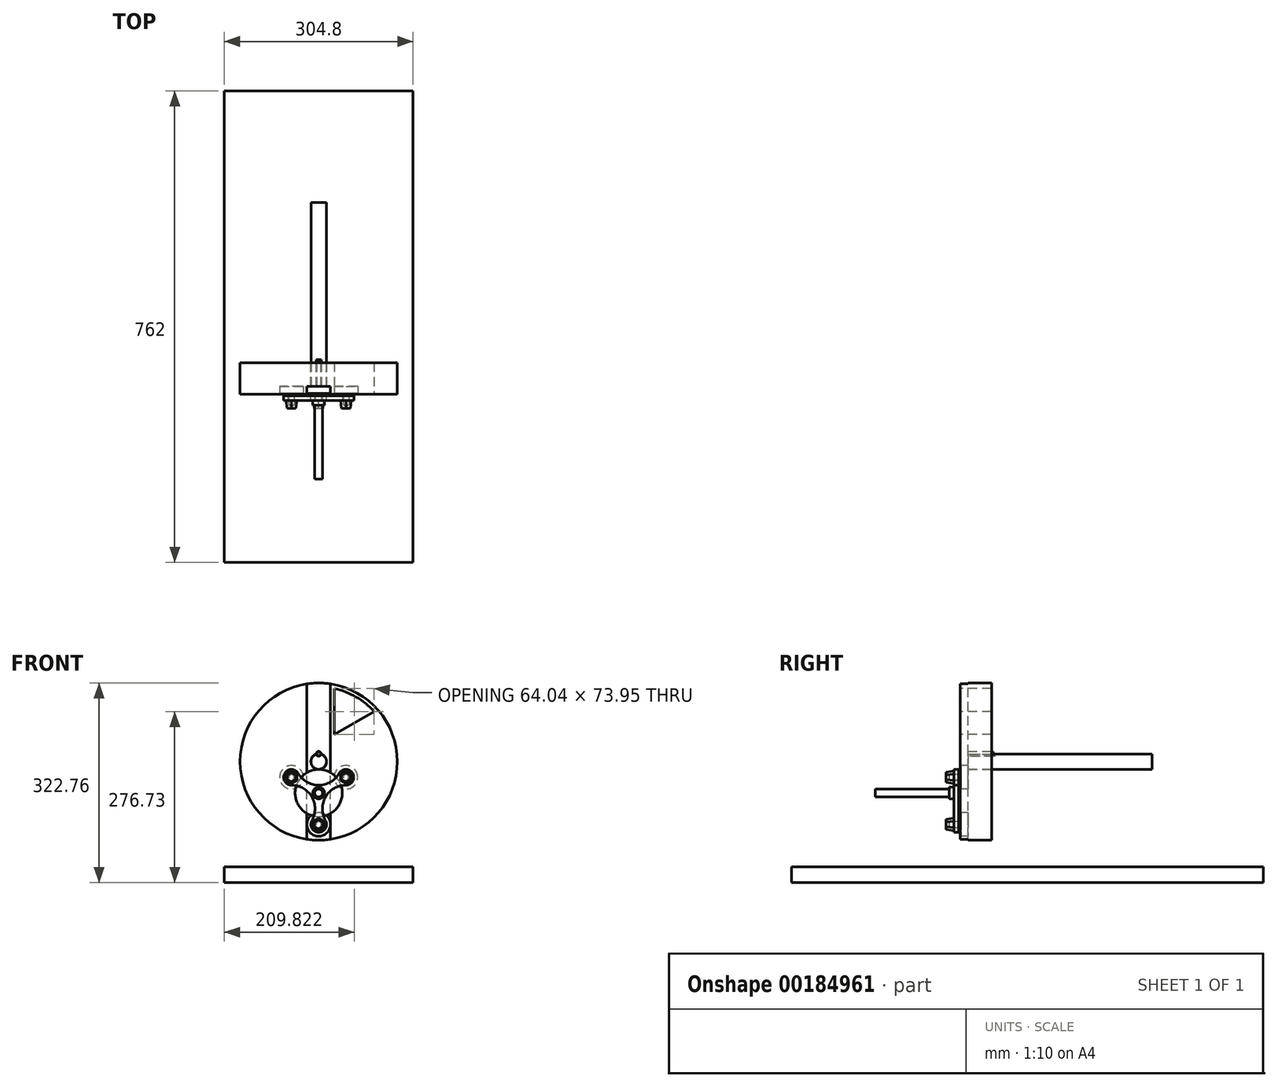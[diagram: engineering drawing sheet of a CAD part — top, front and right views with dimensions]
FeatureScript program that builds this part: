
annotation { "Feature Type Name" : "Feature", "Feature Type Description" : "" }
export const myFeature = defineFeature(function(context is Context, id is Id, definition is map)
    precondition{}
    {
        {
            var Q0;
            Q0=qCreatedBy(makeId("Front.planeOp"),FACE);
            var sketch = newSketch(context, id + "F0", { "sketchPlane" : qUnion([Q0])});
            skCircle(sketch, "E0", {"center": v(0, 0) * mm, "radius": 127 * mm});
            skLineSegment(sketch, "E1", {"start": v(0, 0) * mm, "end": v(0, 12.7) * mm, "construction": true});
            skArc(sketch, "E2", {"start": v(-3.77, 12.13) * mm, "mid": v(0, -12.7) * mm, "end": v(3.77, 12.13) * mm});
            skArc(sketch, "E3", {"start": v(3.77, 12.13) * mm, "mid": v(0, 12.7) * mm, "end": v(-3.77, 12.13) * mm, "construction": true});
            skArc(sketch, "E4", {"start": v(-3.77, 12.13) * mm, "mid": v(0, 8.9) * mm, "end": v(3.77, 12.13) * mm, "construction": true});
            skArc(sketch, "E5", {"start": v(3.77, 12.13) * mm, "mid": v(0, 16.51) * mm, "end": v(-3.77, 12.13) * mm});
            skSolve(sketch);
        }
        {
            var Q0;
            Q0 = qSketchRegion(id + "F0", true);
            extrude(context, id + "F1", {"entities" : qUnion([Q0]), "depth" : 50.8 * mm});
        }
        {
            var Q0;
            Q0=makeQuery(id+"F1.opExtrude","CAP_FACE",FACE,{"disambiguationData":[OSD([sQuery(id+"F0.wireOp",EDGE,"E0")])],"isStart":false});
            var sketch = newSketch(context, id + "F2", { "sketchPlane" : qUnion([Q0])});
            skLineSegment(sketch, "E6", {"start": v(0, -127) * mm, "end": v(0, 147.94) * mm, "construction": true});
            skLineSegment(sketch, "E7.bottom", {"start": v(-19.05, -127) * mm, "end": v(19.05, -127) * mm});
            skLineSegment(sketch, "E7.top", {"start": v(-19.05, 127) * mm, "end": v(19.05, 127) * mm});
            skLineSegment(sketch, "E7.left", {"start": v(-19.05, -127) * mm, "end": v(-19.05, 127) * mm});
            skLineSegment(sketch, "E7.right", {"start": v(19.05, -127) * mm, "end": v(19.05, 127) * mm});
            skSolve(sketch);
        }
        {
            var Q0;
            Q0 = qSketchRegion(id + "F2", true);
            extrude(context, id + "F3", {"entities" : qUnion([Q0]), "operationType" : NewBodyOperationType.REMOVE, "oppositeDirection" : true, "depth" : 12.7 * mm});
        }
        {
            var Q0;
            Q0=qCreatedBy(makeId("Right.planeOp"),FACE);
            var sketch = newSketch(context, id + "F4", { "sketchPlane" : qUnion([Q0])});
            skLineSegment(sketch, "E8", {"start": v(0, 0) * mm, "end": v(-240.38, 0) * mm, "construction": true});
            skSolve(sketch);
        }
        {
            var Q0;
            {var subQ0=sQuery(id+"F0.wireOp",EDGE,"E0");var subQ2=sQuery(id+"F2.wireOp",EDGE,"E7.right");var subQ3=makeQuery(id+"F3.opExtrude","SWEPT_FACE",FACE,{"disambiguationData":[OSD([subQ2])]});var subQ4=makeQuery(id+"F3.boolean.opBoolean","COPY",FACE,{"derivedFrom":subQ3});Q0=makeQuery(id+"FbrtEuTQLlTCqle_1.2.F3.boolean.opBoolean","SPLIT",FACE,{"disambiguationData":[TD([subQ4])],"derivedFrom":makeQuery(id+"FbrtEuTQLlTCqle_1.1.F3.boolean.opBoolean","SPLIT",FACE,{"disambiguationData":[TD([makeQuery(id+"FbrtEuTQLlTCqle_1.1.F3.opExtrude","SWEPT_FACE",FACE,{"disambiguationData":[OSD([sQuery(id+"F2.wireOp",EDGE,"E7.left")])]})])],"derivedFrom":makeQuery(id+"F3.boolean.opBoolean","SPLIT",FACE,{"disambiguationData":[TD([subQ3])],"derivedFrom":makeQuery(id+"F1.opExtrude","CAP_FACE",FACE,{"disambiguationData":[OSD([subQ0])],"isStart":false})})})});}
            var sketch = newSketch(context, id + "F5", { "sketchPlane" : qUnion([Q0])});
            skArc(sketch, "E9.0", {"start": v(89.44, 80.97) * mm, "mid": v(60.32, 104.49) * mm, "end": v(25.4, 117.95) * mm});
            skLineSegment(sketch, "E9.1", {"start": v(89.44, 80.97) * mm, "end": v(25.4, 44) * mm});
            skLineSegment(sketch, "E9.2", {"start": v(25.4, 44) * mm, "end": v(25.4, 117.95) * mm});
            skSolve(sketch);
        }
        {
            var Q0;
            Q0 = qSketchRegion(id + "F5", true);
            extrude(context, id + "F6", {"entities" : qUnion([Q0]), "operationType" : NewBodyOperationType.REMOVE, "endBound" : BoundingType.THROUGH_ALL, "oppositeDirection" : true, "depth" : 25.4 * mm});
        }
        {
            var Q0;
            {var subQ0=sQuery(id+"F0.wireOp",EDGE,"E0");var subQ2=sQuery(id+"F2.wireOp",EDGE,"E7.right");var subQ3=makeQuery(id+"F3.opExtrude","SWEPT_FACE",FACE,{"disambiguationData":[OSD([subQ2])]});var subQ5=sQuery(id+"F2.wireOp",EDGE,"E7.left");var subQ8=makeQuery(id+"F1.opExtrude","CAP_FACE",FACE,{"disambiguationData":[OSD([subQ0])],"isStart":false});var subQ9=makeQuery(id+"FbrtEuTQLlTCqle_1.1.F3.opExtrude","SWEPT_FACE",FACE,{"disambiguationData":[OSD([subQ5])]});Q0=makeQuery(id+"FbrtEuTQLlTCqle_1.2.F3.boolean.opBoolean","SPLIT",FACE,{"disambiguationData":[TD([makeQuery(id+"FbrtEuTQLlTCqle_1.2.F3.opExtrude","SWEPT_FACE",FACE,{"disambiguationData":[OSD([subQ5])]})])],"derivedFrom":makeQuery(id+"FbrtEuTQLlTCqle_1.1.F3.boolean.opBoolean","SPLIT",FACE,{"disambiguationData":[TD([subQ9])],"derivedFrom":makeQuery(id+"F3.boolean.opBoolean","SPLIT",FACE,{"disambiguationData":[TD([subQ3])],"derivedFrom":subQ8})})});}
            var sketch = newSketch(context, id + "F7", { "sketchPlane" : qUnion([Q0])});
            skCircle(sketch, "E10", {"center": v(0, -50.8) * mm, "radius": 38.1 * mm});
            skLineSegment(sketch, "E11", {"start": v(0, 0) * mm, "end": v(278.78, -160.95) * mm, "construction": true});
            skLineSegment(sketch, "E12", {"start": v(0, 0) * mm, "end": v(0, -50.8) * mm, "construction": true});
            skLineSegment(sketch, "E13", {"start": v(0, 0) * mm, "end": v(-197.73, -114.16) * mm, "construction": true});
            skLineSegment(sketch, "E14", {"start": v(0, -50.8) * mm, "end": v(44, -25.4) * mm, "construction": true});
            skLineSegment(sketch, "E15", {"start": v(0, -50.8) * mm, "end": v(-44, -25.4) * mm, "construction": true});
            skLineSegment(sketch, "E16", {"start": v(0, -50.8) * mm, "end": v(0, -101.6) * mm, "construction": true});
            skSolve(sketch);
        }
        {
            var Q0;
            Q0 = qSketchRegion(id + "F7", true);
            extrude(context, id + "F8", {"entities" : qUnion([Q0]), "depth" : 2.54 * mm});
        }
        {
            var Q0;
            Q0=makeQuery(id+"F8.opExtrude","CAP_FACE",FACE,{"disambiguationData":[OSD([sQuery(id+"F7.wireOp",EDGE,"E10")])],"isStart":false});
            var sketch = newSketch(context, id + "F9", { "sketchPlane" : qUnion([Q0])});
            skLineSegment(sketch, "E17.0", {"start": v(0, 0) * mm, "end": v(-197.73, -114.16) * mm, "construction": true});
            skLineSegment(sketch, "E18.0", {"start": v(0, 0) * mm, "end": v(278.78, -160.95) * mm, "construction": true});
            skLineSegment(sketch, "E19.0", {"start": v(0, -50.8) * mm, "end": v(44, -25.4) * mm, "construction": true});
            skCircle(sketch, "E20.0", {"center": v(0, -50.8) * mm, "radius": 38.1 * mm, "construction": true});
            skLineSegment(sketch, "E21.0", {"start": v(0, -50.8) * mm, "end": v(-44, -25.4) * mm, "construction": true});
            skLineSegment(sketch, "E22.0", {"start": v(0, -50.8) * mm, "end": v(0, -101.6) * mm, "construction": true});
            skCircle(sketch, "E23", {"center": v(-44, -25.4) * mm, "radius": 12.7 * mm});
            skCircle(sketch, "E24", {"center": v(44, -25.4) * mm, "radius": 12.7 * mm});
            skCircle(sketch, "E25", {"center": v(0, -101.6) * mm, "radius": 12.7 * mm});
            skArc(sketch, "E26", {"start": v(-33, -19.05) * mm, "mid": v(0, -38.1) * mm, "end": v(33, -19.05) * mm});
            skArc(sketch, "E27", {"start": v(44, -38.1) * mm, "mid": v(11, -57.15) * mm, "end": v(11, -95.25) * mm});
            skArc(sketch, "E28", {"start": v(-11, -95.25) * mm, "mid": v(-11, -57.15) * mm, "end": v(-44, -38.1) * mm});
            skCircle(sketch, "E29", {"center": v(44, -25.4) * mm, "radius": 5.08 * mm});
            skCircle(sketch, "E30", {"center": v(0, -101.6) * mm, "radius": 5.08 * mm});
            skCircle(sketch, "E31", {"center": v(-44, -25.4) * mm, "radius": 5.08 * mm});
            skSolve(sketch);
        }
        {
            var Q0;
            Q0 = qSketchRegion(id + "F9", true);
            extrude(context, id + "F10", {"entities" : qUnion([Q0]), "depth" : 7.62 * mm});
        }
        {
            var Q0;
            Q0=qCreatedBy(makeId("Right.planeOp"),FACE);
            var sketch = newSketch(context, id + "F11", { "sketchPlane" : qUnion([Q0])});
            skLineSegment(sketch, "E32", {"start": v(-50.8, -50.8) * mm, "end": v(-241.02, -50.8) * mm, "construction": true});
            skLineSegment(sketch, "E33", {"start": v(-60.96, -50.8) * mm, "end": v(-60.96, -41.28) * mm});
            skLineSegment(sketch, "E34", {"start": v(-60.96, -41.28) * mm, "end": v(-68.58, -41.28) * mm});
            skLineSegment(sketch, "E35", {"start": v(-68.58, -41.28) * mm, "end": v(-68.58, -44.45) * mm});
            skLineSegment(sketch, "E36", {"start": v(-68.58, -44.45) * mm, "end": v(-187.96, -44.45) * mm});
            skLineSegment(sketch, "E37", {"start": v(-187.96, -44.45) * mm, "end": v(-187.96, -50.8) * mm});
            skLineSegment(sketch, "E38", {"start": v(-187.96, -50.8) * mm, "end": v(-60.96, -50.8) * mm});
            skSolve(sketch);
        }
        {
            var Q0;
            Q0 = qSketchRegion(id + "F11", true);
            var Q1;
            Q1=sQuery(id+"F11.wireOp",EDGE,"E32");
            revolve(context, id + "F12", {"operationType" : NewBodyOperationType.ADD, "entities" : qUnion([Q0]), "axis" : qUnion([Q1]), "revolveType" : RevolveType.FULL});
        }
        {
            var Q0;
            Q0=sQuery(id+"F7.wireOp",VERTEX,"E14.end");
            var Q1;
            Q1=sQuery(id+"F7.wireOp",EDGE,"E11");
            cPlane(context, id + "F13", {"entities" : qUnion([Q0, Q1]), "cplaneType" : CPlaneType.LINE_POINT, "offset" : 25.4 * mm, "width" : 152.4 * mm, "height" : 152.4 * mm});
        }
        {
            var Q0;
            Q0=qCreatedBy(id+"F13.planeOp",FACE);
            var sketch = newSketch(context, id + "F14", { "sketchPlane" : qUnion([Q0])});
            skLineSegment(sketch, "E39", {"start": v(-38.1, 0) * mm, "end": v(-38.1, 19.05) * mm});
            skLineSegment(sketch, "E40", {"start": v(-38.1, 19.05) * mm, "end": v(-49.53, 19.05) * mm});
            skLineSegment(sketch, "E41", {"start": v(-49.53, 19.05) * mm, "end": v(-49.53, 8.9) * mm});
            skLineSegment(sketch, "E42", {"start": v(-49.53, 8.9) * mm, "end": v(-53.34, 8.9) * mm});
            skLineSegment(sketch, "E43", {"start": v(-53.34, 8.9) * mm, "end": v(-53.34, 4.45) * mm});
            skLineSegment(sketch, "E44", {"start": v(-53.34, 4.45) * mm, "end": v(-68.58, 4.44) * mm});
            skLineSegment(sketch, "E45", {"start": v(-68.58, 4.44) * mm, "end": v(-68.58, 0) * mm});
            skLineSegment(sketch, "E46", {"start": v(-68.58, 0) * mm, "end": v(-38.1, 0) * mm});
            skLineSegment(sketch, "E47", {"start": v(-38.1, 0) * mm, "end": v(-22.87, 0) * mm, "construction": true});
            skSolve(sketch);
        }
        {
            var Q0;
            Q0 = qSketchRegion(id + "F14", true);
            var Q1;
            Q1=sQuery(id+"F14.wireOp",EDGE,"E47");
            revolve(context, id + "F15", {"entities" : qUnion([Q0]), "axis" : qUnion([Q1]), "revolveType" : RevolveType.FULL});
        }
        {
            var Q0;
            Q0=makeQuery(id+"F10.opExtrude","CAP_FACE",FACE,{"disambiguationData":[OSD([sQuery(id+"F9.wireOp",EDGE,"E23"),sQuery(id+"F9.wireOp",EDGE,"E24"),sQuery(id+"F9.wireOp",EDGE,"E25"),sQuery(id+"F9.wireOp",EDGE,"E26"),sQuery(id+"F9.wireOp",EDGE,"E27"),sQuery(id+"F9.wireOp",EDGE,"E28"),sQuery(id+"F9.wireOp",EDGE,"E29"),sQuery(id+"F9.wireOp",EDGE,"E30"),sQuery(id+"F9.wireOp",EDGE,"E31")])],"isStart":false});
            var sketch = newSketch(context, id + "F16", { "sketchPlane" : qUnion([Q0])});
            skCircle(sketch, "E48", {"center": v(44, -25.4) * mm, "radius": 10.16 * mm, "construction": true});
            skLineSegment(sketch, "E49", {"start": v(44, -15.24) * mm, "end": v(44, -35.56) * mm, "construction": true});
            skLineSegment(sketch, "E50", {"start": v(35.2, -20.32) * mm, "end": v(52.8, -30.48) * mm, "construction": true});
            skLineSegment(sketch, "E51", {"start": v(35.2, -30.48) * mm, "end": v(52.8, -20.32) * mm, "construction": true});
            skLineSegment(sketch, "E52", {"start": v(35.2, -20.32) * mm, "end": v(44, -15.24) * mm});
            skLineSegment(sketch, "E53", {"start": v(44, -15.24) * mm, "end": v(52.8, -20.32) * mm});
            skLineSegment(sketch, "E54", {"start": v(52.8, -20.32) * mm, "end": v(52.8, -30.48) * mm});
            skLineSegment(sketch, "E55", {"start": v(52.8, -30.48) * mm, "end": v(44, -35.56) * mm});
            skLineSegment(sketch, "E56", {"start": v(44, -35.56) * mm, "end": v(35.2, -30.48) * mm});
            skLineSegment(sketch, "E57", {"start": v(35.2, -30.48) * mm, "end": v(35.2, -20.32) * mm});
            skSolve(sketch);
        }
        {
            var Q0;
            Q0 = qSketchRegion(id + "F16", true);
            extrude(context, id + "F17", {"entities" : qUnion([Q0]), "depth" : 12.7 * mm, "hasDraft" : true, "draftAngle" : 8 * degree, "draftPullDirection" : true});
        }
        {
            var Q0;
            Q0=makeQuery(id+"F17.opExtrude","SWEPT_BODY",BODY,{"disambiguationData":[OSD([sQuery(id+"F16.wireOp",EDGE,"E52"),sQuery(id+"F16.wireOp",EDGE,"E53"),sQuery(id+"F16.wireOp",EDGE,"E54"),sQuery(id+"F16.wireOp",EDGE,"E55"),sQuery(id+"F16.wireOp",EDGE,"E56"),sQuery(id+"F16.wireOp",EDGE,"E57")])]});
            var Q1;
            Q1=makeQuery(id+"F15.opRevolve","SWEPT_BODY",BODY,{"disambiguationData":[OSD([sQuery(id+"F14.wireOp",EDGE,"E39"),sQuery(id+"F14.wireOp",EDGE,"E40"),sQuery(id+"F14.wireOp",EDGE,"E41"),sQuery(id+"F14.wireOp",EDGE,"E42"),sQuery(id+"F14.wireOp",EDGE,"E43"),sQuery(id+"F14.wireOp",EDGE,"E44"),sQuery(id+"F14.wireOp",EDGE,"E45"),sQuery(id+"F14.wireOp",EDGE,"E46")])]});
            var Q2;
            Q2=sQuery(id+"F11.wireOp",EDGE,"E32");
            circularPattern(context, id + "F18", {"entities" : qUnion([Q0, Q1]), "axis" : qUnion([Q2]), "angle" : 360 * degree, "instanceCount" : 3, "equalSpace" : true});
        }
        {
            var Q0;
            {var subQ0=sQuery(id+"F2.wireOp",EDGE,"E7.right");var subQ1=sQuery(id+"F2.wireOp",EDGE,"E7.left");var subQ2=sQuery(id+"F2.wireOp",EDGE,"E7.top");var subQ3=sQuery(id+"F2.wireOp",EDGE,"E7.bottom");Q0=makeQuery(id+"FbrtEuTQLlTCqle_1.2.F3.boolean.opBoolean","MERGE",FACE,{"derivedFrom":[makeQuery(id+"FbrtEuTQLlTCqle_1.1.F3.boolean.opBoolean","MERGE",FACE,{"derivedFrom":[makeQuery(id+"F3.boolean.opBoolean","COPY",FACE,{"derivedFrom":makeQuery(id+"F3.opExtrude","CAP_FACE",FACE,{"disambiguationData":[OSD([subQ3,subQ2,subQ1,subQ0])],"isStart":false})}),makeQuery(id+"FbrtEuTQLlTCqle_1.1.F3.opExtrude","CAP_FACE",FACE,{"disambiguationData":[OSD([subQ3,subQ2,subQ1,subQ0])],"isStart":false})]}),makeQuery(id+"FbrtEuTQLlTCqle_1.2.F3.opExtrude","CAP_FACE",FACE,{"disambiguationData":[OSD([subQ3,subQ2,subQ1,subQ0])],"isStart":false})]});}
            var sketch = newSketch(context, id + "F19", { "sketchPlane" : qUnion([Q0])});
            skArc(sketch, "E58.0", {"start": v(-3.96, 11.8) * mm, "mid": v(0, 8.64) * mm, "end": v(3.96, 11.8) * mm});
            skArc(sketch, "E58.1", {"start": v(-3.96, 11.8) * mm, "mid": v(0, -12.45) * mm, "end": v(3.96, 11.8) * mm});
            skSolve(sketch);
        }
        {
            var Q0;
            Q0 = qSketchRegion(id + "F19", true);
            extrude(context, id + "F20", {"entities" : qUnion([Q0]), "oppositeDirection" : true, "depth" : 43.18 * mm});
        }
        {
            var Q0;
            Q0=makeQuery(id+"F20.opExtrude","CAP_FACE",FACE,{"disambiguationData":[OSD([sQuery(id+"F19.wireOp",EDGE,"E58.0"),sQuery(id+"F19.wireOp",EDGE,"E58.1")])],"isStart":false});
            var sketch = newSketch(context, id + "F21", { "sketchPlane" : qUnion([Q0])});
            skCircle(sketch, "E59", {"center": v(0, 0) * mm, "radius": 12.45 * mm});
            skSolve(sketch);
        }
        {
            var Q0;
            Q0 = qSketchRegion(id + "F21", true);
            extrude(context, id + "F22", {"entities" : qUnion([Q0]), "operationType" : NewBodyOperationType.ADD, "depth" : 254 * mm});
        }
        {
            var Q0;
            {var subQ0=sQuery(id+"F2.wireOp",EDGE,"E7.right");var subQ1=sQuery(id+"F2.wireOp",EDGE,"E7.left");var subQ2=sQuery(id+"F2.wireOp",EDGE,"E7.top");var subQ3=sQuery(id+"F2.wireOp",EDGE,"E7.bottom");Q0=makeQuery(id+"FbrtEuTQLlTCqle_1.2.F3.boolean.opBoolean","MERGE",FACE,{"derivedFrom":[makeQuery(id+"FbrtEuTQLlTCqle_1.1.F3.boolean.opBoolean","MERGE",FACE,{"derivedFrom":[makeQuery(id+"F3.boolean.opBoolean","COPY",FACE,{"derivedFrom":makeQuery(id+"F3.opExtrude","CAP_FACE",FACE,{"disambiguationData":[OSD([subQ3,subQ2,subQ1,subQ0])],"isStart":false})}),makeQuery(id+"FbrtEuTQLlTCqle_1.1.F3.opExtrude","CAP_FACE",FACE,{"disambiguationData":[OSD([subQ3,subQ2,subQ1,subQ0])],"isStart":false})]}),makeQuery(id+"FbrtEuTQLlTCqle_1.2.F3.opExtrude","CAP_FACE",FACE,{"disambiguationData":[OSD([subQ3,subQ2,subQ1,subQ0])],"isStart":false})]});}
            var sketch = newSketch(context, id + "F23", { "sketchPlane" : qUnion([Q0])});
            skCircle(sketch, "E60", {"center": v(0, 12.7) * mm, "radius": 3.56 * mm});
            skSolve(sketch);
        }
        {
            var Q0;
            Q0 = qSketchRegion(id + "F23", true);
            extrude(context, id + "F24", {"entities" : qUnion([Q0]), "oppositeDirection" : true, "depth" : 40.64 * mm});
        }
        {
            var Q0;
            Q0=qCreatedBy(makeId("Right.planeOp"),FACE);
            var sketch = newSketch(context, id + "F25", { "sketchPlane" : qUnion([Q0])});
            skLineSegment(sketch, "E61.bottom", {"start": v(439.33, -170.36) * mm, "end": v(-322.67, -170.36) * mm});
            skLineSegment(sketch, "E61.top", {"start": v(439.33, -195.76) * mm, "end": v(-322.67, -195.76) * mm});
            skLineSegment(sketch, "E61.left", {"start": v(439.33, -170.36) * mm, "end": v(439.33, -195.76) * mm});
            skLineSegment(sketch, "E61.right", {"start": v(-322.67, -170.36) * mm, "end": v(-322.67, -195.76) * mm});
            skLineSegment(sketch, "E62", {"start": v(-322.67, -170.36) * mm, "end": v(-322.67, -50.8) * mm, "construction": true});
            skLineSegment(sketch, "E63", {"start": v(-322.67, -50.8) * mm, "end": v(-266.34, -50.8) * mm, "construction": true});
            skLineSegment(sketch, "E64", {"start": v(439.33, -170.36) * mm, "end": v(439.33, 0) * mm, "construction": true});
            skLineSegment(sketch, "E65", {"start": v(439.33, 0) * mm, "end": v(334.76, 0) * mm, "construction": true});
            skSolve(sketch);
        }
        {
            var Q0;
            Q0 = qSketchRegion(id + "F25", true);
            extrude(context, id + "F26", {"entities" : qUnion([Q0]), "endBound" : BoundingType.SYMMETRIC, "depth" : 304.8 * mm});
        }
    });
